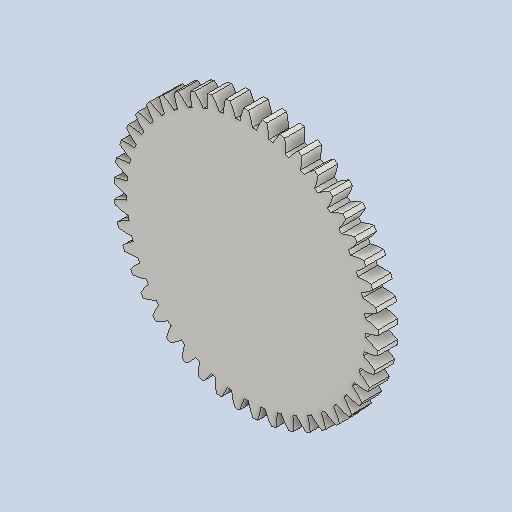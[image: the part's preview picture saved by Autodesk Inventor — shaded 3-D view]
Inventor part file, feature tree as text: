
AUTODESK INVENTOR PART (.ipt)
format: ipt  version: 2025.2 (Build 292293000, 293)  size: 321,024 bytes
history: native  units: mm (DEFAULTED — no unit token found)
features: plane x3, other x3, extrude x1, sketch x1
ambient origin geometry x8: Origin, YZ Plane, XZ Plane, XY Plane, X Axis, Y Axis, Z Axis, Center Point
bodies: Solid1 (feature_tree)
feature tree (8):
  extrude  "Extrusion1"  Depth=7.0mm TaperAngle=0.0deg
  plane  "Work Plane2"
  plane  "Work Plane8"
  plane  "Work Plane9"
  other  "Spur Gear"
  sketch  "Sketch1"  dims[d0=94.0mm d1=7.0mm d2=0.0mm d3=90.0mm d4=10.0mm d5=0.0mm d16=60.0mm d17=0.0mm d34=0.698132mm d39=0.0mm d41=0.0mm d43=60.0mm d46=60.0mm d47=0.0mm d48=0.0mm]
  other  "Srf1"
  other  "Pitch Diameter"
